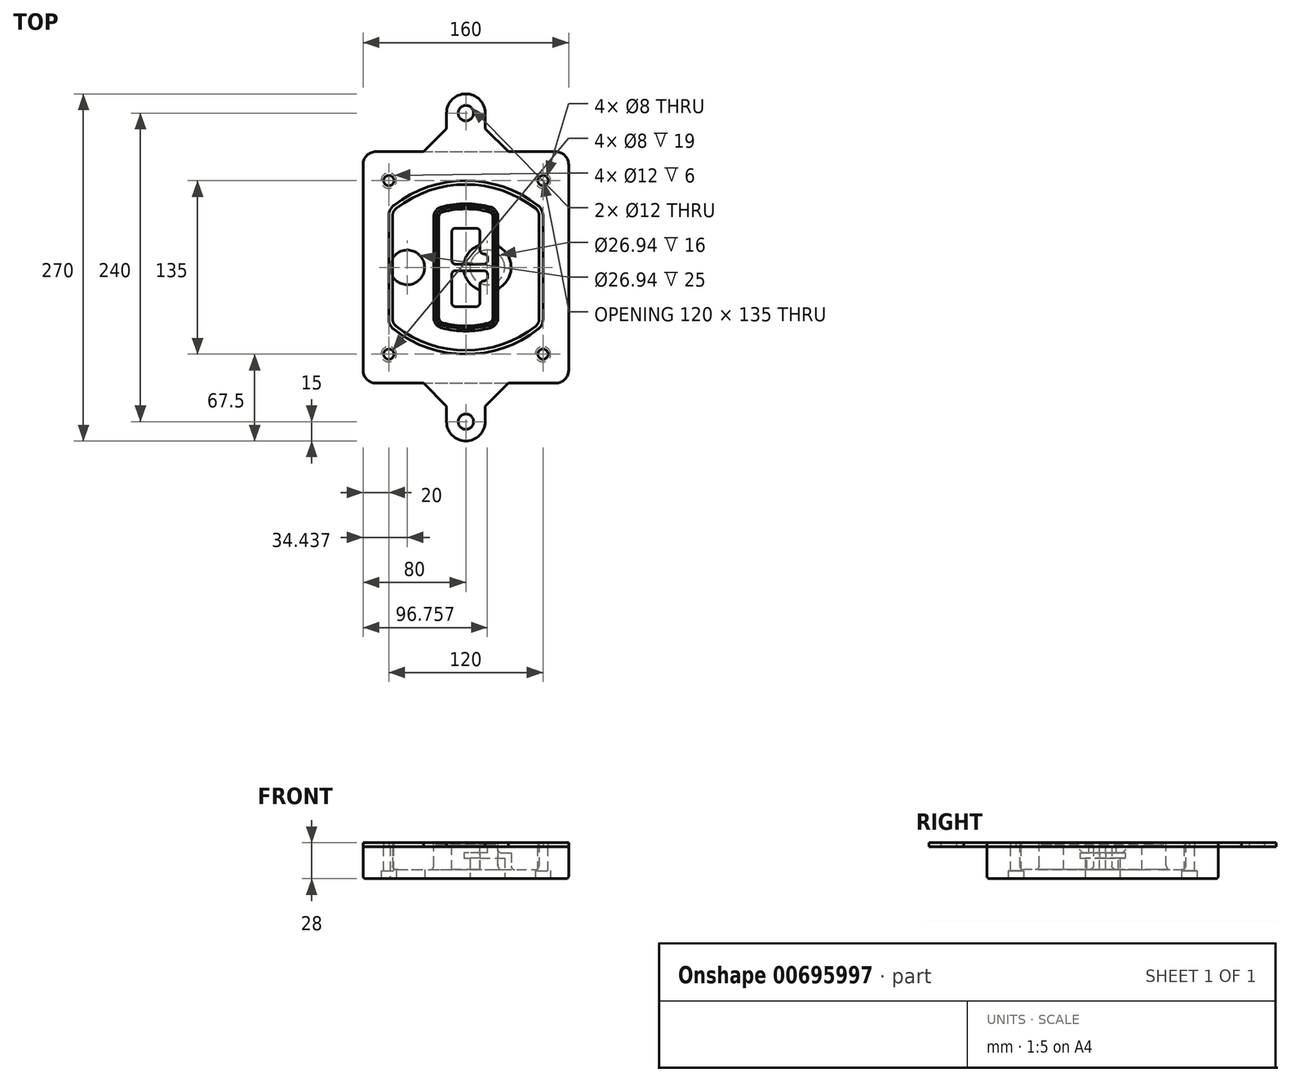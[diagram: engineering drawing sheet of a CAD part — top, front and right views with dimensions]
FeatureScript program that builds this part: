
annotation { "Feature Type Name" : "Feature", "Feature Type Description" : "" }
export const myFeature = defineFeature(function(context is Context, id is Id, definition is map)
    precondition{}
    {
        {
            var Q0;
            Q0=qCreatedBy(makeId("Top.planeOp"),FACE);
            var sketch = newSketch(context, id + "F0", { "sketchPlane" : qUnion([Q0])});
            skPoint(sketch, "E0.rect.middle", {"position": v(0, 0) * mm});
            skLineSegment(sketch, "E1.bottom", {"start": v(-70, -90) * mm, "end": v(70, -90) * mm});
            skLineSegment(sketch, "E1.top", {"start": v(-70, 90) * mm, "end": v(70, 90) * mm});
            skLineSegment(sketch, "E1.left", {"start": v(-80, -80) * mm, "end": v(-80, 80) * mm});
            skLineSegment(sketch, "E1.right", {"start": v(80, -80) * mm, "end": v(80, 80) * mm});
            skLineSegment(sketch, "E2", {"start": v(-80, 90) * mm, "end": v(80, -90) * mm, "construction": true});
            skLineSegment(sketch, "E3", {"start": v(80, 90) * mm, "end": v(-80, -90) * mm, "construction": true});
            skCircle(sketch, "E4", {"center": v(-60, 67.5) * mm, "radius": 4 * mm});
            skCircle(sketch, "E5", {"center": v(60, 67.5) * mm, "radius": 4 * mm});
            skCircle(sketch, "E6", {"center": v(60, -67.5) * mm, "radius": 4 * mm});
            skCircle(sketch, "E7", {"center": v(-60, -67.5) * mm, "radius": 4 * mm});
            skLineSegment(sketch, "E8", {"start": v(-60, 67.5) * mm, "end": v(60, 67.5) * mm, "construction": true});
            skLineSegment(sketch, "E9", {"start": v(60, 67.5) * mm, "end": v(60, -67.5) * mm, "construction": true});
            skLineSegment(sketch, "E10", {"start": v(60, -67.5) * mm, "end": v(-60, -67.5) * mm, "construction": true});
            skLineSegment(sketch, "E11", {"start": v(-60, -67.5) * mm, "end": v(-60, 67.5) * mm, "construction": true});
            skLineSegment(sketch, "E12", {"start": v(-60, 40.3) * mm, "end": v(-60, -40.3) * mm});
            skLineSegment(sketch, "E13", {"start": v(60, 40.3) * mm, "end": v(60, -40.3) * mm});
            skArc(sketch, "E14", {"start": v(56.15, 48.18) * mm, "mid": v(0, 67.5) * mm, "end": v(-56.15, 48.18) * mm});
            skArc(sketch, "E15", {"start": v(-56.15, -48.18) * mm, "mid": v(0, -67.5) * mm, "end": v(56.15, -48.18) * mm});
            skLineSegment(sketch, "E16", {"start": v(-60, 0) * mm, "end": v(60, 0) * mm, "construction": true});
            skPoint(sketch, "E17.visualSharp", {"position": v(-60, -45) * mm});
            skArc(sketch, "E17.filletArc", {"start": v(-60, -40.3) * mm, "mid": v(-58.99, -44.68) * mm, "end": v(-56.15, -48.18) * mm});
            skPoint(sketch, "E18.visualSharp", {"position": v(-60, 45) * mm});
            skArc(sketch, "E18.filletArc", {"start": v(-56.15, 48.18) * mm, "mid": v(-58.99, 44.68) * mm, "end": v(-60, 40.3) * mm});
            skPoint(sketch, "E19.visualSharp", {"position": v(60, 45) * mm});
            skArc(sketch, "E19.filletArc", {"start": v(60, 40.3) * mm, "mid": v(58.99, 44.68) * mm, "end": v(56.15, 48.18) * mm});
            skPoint(sketch, "E20.visualSharp", {"position": v(60, -45) * mm});
            skArc(sketch, "E20.filletArc", {"start": v(56.15, -48.18) * mm, "mid": v(58.99, -44.68) * mm, "end": v(60, -40.3) * mm});
            skPoint(sketch, "E21.visualSharp", {"position": v(-80, 90) * mm});
            skArc(sketch, "E21.filletArc", {"start": v(-70, 90) * mm, "mid": v(-77.07, 87.07) * mm, "end": v(-80, 80) * mm});
            skPoint(sketch, "E22.visualSharp", {"position": v(80, 90) * mm});
            skArc(sketch, "E22.filletArc", {"start": v(80, 80) * mm, "mid": v(77.07, 87.07) * mm, "end": v(70, 90) * mm});
            skPoint(sketch, "E23.visualSharp", {"position": v(80, -90) * mm});
            skArc(sketch, "E23.filletArc", {"start": v(70, -90) * mm, "mid": v(77.07, -87.07) * mm, "end": v(80, -80) * mm});
            skPoint(sketch, "E24.visualSharp", {"position": v(-80, -90) * mm});
            skArc(sketch, "E24.filletArc", {"start": v(-80, -80) * mm, "mid": v(-77.07, -87.07) * mm, "end": v(-70, -90) * mm});
            skArc(sketch, "E25.0", {"start": v(57, 40.3) * mm, "mid": v(56.3, 43.36) * mm, "end": v(54.3, 45.81) * mm});
            skLineSegment(sketch, "E25.1", {"start": v(57, 40.3) * mm, "end": v(57, -40.3) * mm});
            skArc(sketch, "E25.2", {"start": v(54.3, -45.81) * mm, "mid": v(56.3, -43.36) * mm, "end": v(57, -40.3) * mm});
            skArc(sketch, "E25.3", {"start": v(-54.3, -45.81) * mm, "mid": v(0, -64.5) * mm, "end": v(54.3, -45.81) * mm});
            skArc(sketch, "E25.4", {"start": v(-57, -40.3) * mm, "mid": v(-56.3, -43.36) * mm, "end": v(-54.3, -45.81) * mm});
            skArc(sketch, "E25.5", {"start": v(54.3, 45.81) * mm, "mid": v(0, 64.5) * mm, "end": v(-54.3, 45.81) * mm});
            skLineSegment(sketch, "E25.6", {"start": v(-57, 40.3) * mm, "end": v(-57, -40.3) * mm});
            skArc(sketch, "E25.7", {"start": v(-54.3, 45.81) * mm, "mid": v(-56.3, 43.36) * mm, "end": v(-57, 40.3) * mm});
            skArc(sketch, "E26.0", {"start": v(-58.62, 51.33) * mm, "mid": v(-62.58, 46.43) * mm, "end": v(-64, 40.3) * mm});
            skArc(sketch, "E26.1", {"start": v(58.62, 51.33) * mm, "mid": v(0, 71.5) * mm, "end": v(-58.62, 51.33) * mm});
            skArc(sketch, "E26.2", {"start": v(64, 40.3) * mm, "mid": v(62.58, 46.43) * mm, "end": v(58.62, 51.33) * mm});
            skLineSegment(sketch, "E26.3", {"start": v(64, 40.3) * mm, "end": v(64, -40.3) * mm});
            skArc(sketch, "E26.4", {"start": v(58.62, -51.33) * mm, "mid": v(62.58, -46.43) * mm, "end": v(64, -40.3) * mm});
            skLineSegment(sketch, "E26.5", {"start": v(-64, 40.3) * mm, "end": v(-64, -40.3) * mm});
            skArc(sketch, "E26.6", {"start": v(-58.62, -51.33) * mm, "mid": v(0, -71.5) * mm, "end": v(58.62, -51.33) * mm});
            skArc(sketch, "E26.7", {"start": v(-64, -40.3) * mm, "mid": v(-62.58, -46.43) * mm, "end": v(-58.62, -51.33) * mm});
            skSolve(sketch);
        }
        {
            var Q0;
            Q0=makeQuery(id+"F0.imprint","IMPRINT",FACE,{"disambiguationData":[TD([[makeQuery(id+"F0.imprint","IMPRINT",EDGE,{"derivedFrom":sQuery(id+"F0.wireOp",EDGE,"E1.bottom")}),1.0]])]});
            var Q1;
            Q1=makeQuery(id+"F0.imprint","IMPRINT",FACE,{"disambiguationData":[TD([[makeQuery(id+"F0.imprint","IMPRINT",EDGE,{"derivedFrom":sQuery(id+"F0.wireOp",EDGE,"E12")}),1.0]])]});
            var Q2;
            Q2=makeQuery(id+"F0.imprint","IMPRINT",FACE,{"disambiguationData":[TD([[makeQuery(id+"F0.imprint","IMPRINT",EDGE,{"derivedFrom":sQuery(id+"F0.wireOp",EDGE,"E25.0")}),1.0]])]});
            var Q3;
            Q3=makeQuery(id+"F0.imprint","IMPRINT",FACE,{"disambiguationData":[TD([[makeQuery(id+"F0.imprint","IMPRINT",EDGE,{"derivedFrom":sQuery(id+"F0.wireOp",EDGE,"E12")}),-1.0]])]});
            extrude(context, id + "F1", {"entities" : qUnion([Q0, Q1, Q2, Q3]), "oppositeDirection" : true, "depth" : 25 * mm});
        }
        {
            var Q0;
            Q0=makeQuery(id+"F0.imprint","IMPRINT",FACE,{"disambiguationData":[TD([[makeQuery(id+"F0.imprint","IMPRINT",EDGE,{"derivedFrom":sQuery(id+"F0.wireOp",EDGE,"E12")}),1.0]])]});
            extrude(context, id + "F2", {"entities" : qUnion([Q0]), "operationType" : NewBodyOperationType.ADD, "depth" : 3 * mm});
        }
        {
            var Q0;
            Q0=makeQuery(id+"F0.imprint","IMPRINT",FACE,{"disambiguationData":[TD([[makeQuery(id+"F0.imprint","IMPRINT",EDGE,{"derivedFrom":sQuery(id+"F0.wireOp",EDGE,"E25.0")}),1.0]])]});
            extrude(context, id + "F3", {"entities" : qUnion([Q0]), "operationType" : NewBodyOperationType.REMOVE, "oppositeDirection" : true, "depth" : 18 * mm});
        }
        {
            var Q0;
            Q0=makeQuery(id+"F2.opExtrude","CAP_FACE",FACE,{"disambiguationData":[OSD([sQuery(id+"F0.wireOp",EDGE,"E12"),sQuery(id+"F0.wireOp",EDGE,"E13"),sQuery(id+"F0.wireOp",EDGE,"E14"),sQuery(id+"F0.wireOp",EDGE,"E15"),sQuery(id+"F0.wireOp",EDGE,"E17.filletArc"),sQuery(id+"F0.wireOp",EDGE,"E18.filletArc"),sQuery(id+"F0.wireOp",EDGE,"E19.filletArc"),sQuery(id+"F0.wireOp",EDGE,"E20.filletArc"),sQuery(id+"F0.wireOp",EDGE,"E25.0"),sQuery(id+"F0.wireOp",EDGE,"E25.1"),sQuery(id+"F0.wireOp",EDGE,"E25.2"),sQuery(id+"F0.wireOp",EDGE,"E25.3"),sQuery(id+"F0.wireOp",EDGE,"E25.4"),sQuery(id+"F0.wireOp",EDGE,"E25.5"),sQuery(id+"F0.wireOp",EDGE,"E25.6"),sQuery(id+"F0.wireOp",EDGE,"E25.7")])],"isStart":false});
            var sketch = newSketch(context, id + "F4", { "sketchPlane" : qUnion([Q0])});
            skArc(sketch, "E27.0", {"start": v(-19.08, -46.97) * mm, "mid": v(0, -49.5) * mm, "end": v(19.08, -46.97) * mm});
            skArc(sketch, "E28.0", {"start": v(19.08, 46.97) * mm, "mid": v(0, 49.5) * mm, "end": v(-19.08, 46.97) * mm});
            skLineSegment(sketch, "E29", {"start": v(-25, 39.25) * mm, "end": v(-25, -39.25) * mm});
            skLineSegment(sketch, "E30", {"start": v(25, 39.25) * mm, "end": v(25, -39.25) * mm});
            skLineSegment(sketch, "E31", {"start": v(-25, 45.1) * mm, "end": v(25, 45.1) * mm, "construction": true});
            skLineSegment(sketch, "E32", {"start": v(-25, -45.1) * mm, "end": v(25, -45.1) * mm, "construction": true});
            skPoint(sketch, "E33.visualSharp", {"position": v(-25, 45.1) * mm});
            skArc(sketch, "E33.filletArc", {"start": v(-19.08, 46.97) * mm, "mid": v(-23.35, 44.11) * mm, "end": v(-25, 39.25) * mm});
            skPoint(sketch, "E34.visualSharp", {"position": v(25, 45.1) * mm});
            skArc(sketch, "E34.filletArc", {"start": v(25, 39.25) * mm, "mid": v(23.35, 44.11) * mm, "end": v(19.08, 46.97) * mm});
            skPoint(sketch, "E35.visualSharp", {"position": v(25, -45.1) * mm});
            skArc(sketch, "E35.filletArc", {"start": v(19.08, -46.97) * mm, "mid": v(23.35, -44.11) * mm, "end": v(25, -39.25) * mm});
            skPoint(sketch, "E36.visualSharp", {"position": v(-25, -45.1) * mm});
            skArc(sketch, "E36.filletArc", {"start": v(-25, -39.25) * mm, "mid": v(-23.35, -44.11) * mm, "end": v(-19.08, -46.97) * mm});
            skArc(sketch, "E37.0", {"start": v(54.3, 45.81) * mm, "mid": v(0, 64.5) * mm, "end": v(-54.3, 45.81) * mm});
            skArc(sketch, "E37.1", {"start": v(-54.3, 45.81) * mm, "mid": v(-56.3, 43.36) * mm, "end": v(-57, 40.3) * mm});
            skLineSegment(sketch, "E37.2", {"start": v(-57, 40.3) * mm, "end": v(-57, -40.3) * mm});
            skArc(sketch, "E37.3", {"start": v(-57, -40.3) * mm, "mid": v(-56.3, -43.36) * mm, "end": v(-54.3, -45.81) * mm});
            skArc(sketch, "E37.4", {"start": v(-54.3, -45.81) * mm, "mid": v(0, -64.5) * mm, "end": v(54.3, -45.81) * mm});
            skArc(sketch, "E37.5", {"start": v(54.3, -45.81) * mm, "mid": v(56.3, -43.36) * mm, "end": v(57, -40.3) * mm});
            skLineSegment(sketch, "E37.6", {"start": v(57, 40.3) * mm, "end": v(57, -40.3) * mm});
            skArc(sketch, "E37.7", {"start": v(57, 40.3) * mm, "mid": v(56.3, 43.36) * mm, "end": v(54.3, 45.81) * mm});
            skLineSegment(sketch, "E38.0", {"start": v(23, 39.25) * mm, "end": v(23, -39.25) * mm});
            skArc(sketch, "E38.1", {"start": v(18.56, -45.04) * mm, "mid": v(21.76, -42.9) * mm, "end": v(23, -39.25) * mm});
            skArc(sketch, "E38.2", {"start": v(-18.56, -45.04) * mm, "mid": v(0, -47.5) * mm, "end": v(18.56, -45.04) * mm});
            skArc(sketch, "E38.3", {"start": v(-23, -39.25) * mm, "mid": v(-21.76, -42.9) * mm, "end": v(-18.56, -45.04) * mm});
            skLineSegment(sketch, "E38.4", {"start": v(-23, 39.25) * mm, "end": v(-23, -39.25) * mm});
            skArc(sketch, "E38.5", {"start": v(23, 39.25) * mm, "mid": v(21.76, 42.9) * mm, "end": v(18.56, 45.04) * mm});
            skArc(sketch, "E38.6", {"start": v(-18.56, 45.04) * mm, "mid": v(-21.76, 42.9) * mm, "end": v(-23, 39.25) * mm});
            skArc(sketch, "E38.7", {"start": v(18.56, 45.04) * mm, "mid": v(0, 47.5) * mm, "end": v(-18.56, 45.04) * mm});
            skArc(sketch, "E39.0", {"start": v(21, 39.25) * mm, "mid": v(20.18, 41.68) * mm, "end": v(18.04, 43.1) * mm});
            skLineSegment(sketch, "E39.1", {"start": v(21, 39.25) * mm, "end": v(21, -39.25) * mm});
            skArc(sketch, "E39.2", {"start": v(18.04, -43.1) * mm, "mid": v(20.18, -41.68) * mm, "end": v(21, -39.25) * mm});
            skArc(sketch, "E39.3", {"start": v(-18.04, -43.1) * mm, "mid": v(0, -45.5) * mm, "end": v(18.04, -43.1) * mm});
            skArc(sketch, "E39.4", {"start": v(-21, -39.25) * mm, "mid": v(-20.18, -41.68) * mm, "end": v(-18.04, -43.1) * mm});
            skArc(sketch, "E39.5", {"start": v(18.04, 43.1) * mm, "mid": v(0, 45.5) * mm, "end": v(-18.04, 43.1) * mm});
            skLineSegment(sketch, "E39.6", {"start": v(-21, 39.25) * mm, "end": v(-21, -39.25) * mm});
            skArc(sketch, "E39.7", {"start": v(-18.04, 43.1) * mm, "mid": v(-20.18, 41.68) * mm, "end": v(-21, 39.25) * mm});
            skLineSegment(sketch, "E40", {"start": v(-25, 0) * mm, "end": v(25, 0) * mm, "construction": true});
            skLineSegment(sketch, "E41", {"start": v(-11, 5.5) * mm, "end": v(-11, 27.5) * mm});
            skLineSegment(sketch, "E42", {"start": v(-8, 30.5) * mm, "end": v(8, 30.5) * mm});
            skLineSegment(sketch, "E43", {"start": v(11, 27.5) * mm, "end": v(11, 13.5) * mm});
            skLineSegment(sketch, "E44", {"start": v(14, 10.5) * mm, "end": v(14, 10.5) * mm});
            skLineSegment(sketch, "E45", {"start": v(17, 7.5) * mm, "end": v(17, 5.5) * mm});
            skLineSegment(sketch, "E46", {"start": v(14, 2.5) * mm, "end": v(-8, 2.5) * mm});
            skPoint(sketch, "E47.visualSharp", {"position": v(-11, 30.5) * mm});
            skArc(sketch, "E47.filletArc", {"start": v(-8, 30.5) * mm, "mid": v(-10.12, 29.62) * mm, "end": v(-11, 27.5) * mm});
            skPoint(sketch, "E48.visualSharp", {"position": v(11, 30.5) * mm});
            skArc(sketch, "E48.filletArc", {"start": v(11, 27.5) * mm, "mid": v(10.12, 29.62) * mm, "end": v(8, 30.5) * mm});
            skPoint(sketch, "E49.visualSharp", {"position": v(11, 10.5) * mm});
            skArc(sketch, "E49.filletArc", {"start": v(11, 13.5) * mm, "mid": v(11.88, 11.38) * mm, "end": v(14, 10.5) * mm});
            skPoint(sketch, "E50.visualSharp", {"position": v(17, 10.5) * mm});
            skArc(sketch, "E50.filletArc", {"start": v(17, 7.5) * mm, "mid": v(16.12, 9.62) * mm, "end": v(14, 10.5) * mm});
            skPoint(sketch, "E51.visualSharp", {"position": v(17, 2.5) * mm});
            skArc(sketch, "E51.filletArc", {"start": v(14, 2.5) * mm, "mid": v(16.12, 3.38) * mm, "end": v(17, 5.5) * mm});
            skPoint(sketch, "E52.visualSharp", {"position": v(-11, 2.5) * mm});
            skArc(sketch, "E52.filletArc", {"start": v(-11, 5.5) * mm, "mid": v(-10.12, 3.38) * mm, "end": v(-8, 2.5) * mm});
            skLineSegment(sketch, "E53.0.MirrorCS", {"start": v(14, -2.5) * mm, "end": v(-8, -2.5) * mm});
            skArc(sketch, "E54.0.MirrorCS", {"start": v(-11, -5.5) * mm, "mid": v(-10.12, -3.38) * mm, "end": v(-8, -2.5) * mm});
            skLineSegment(sketch, "E55.0.MirrorCS", {"start": v(-11, -5.5) * mm, "end": v(-11, -27.5) * mm});
            skArc(sketch, "E56.0.MirrorCS", {"start": v(-8, -30.5) * mm, "mid": v(-10.12, -29.62) * mm, "end": v(-11, -27.5) * mm});
            skLineSegment(sketch, "E57.0.MirrorCS", {"start": v(-8, -30.5) * mm, "end": v(8, -30.5) * mm});
            skArc(sketch, "E58.0.MirrorCS", {"start": v(11, -27.5) * mm, "mid": v(10.12, -29.62) * mm, "end": v(8, -30.5) * mm});
            skLineSegment(sketch, "E59.0.MirrorCS", {"start": v(11, -27.5) * mm, "end": v(11, -13.5) * mm});
            skArc(sketch, "E60.0.MirrorCS", {"start": v(11, -13.5) * mm, "mid": v(11.88, -11.38) * mm, "end": v(14, -10.5) * mm});
            skArc(sketch, "E61.0.MirrorCS", {"start": v(17, -7.5) * mm, "mid": v(16.12, -9.62) * mm, "end": v(14, -10.5) * mm});
            skLineSegment(sketch, "E62.0.MirrorCS", {"start": v(17, -7.5) * mm, "end": v(17, -5.5) * mm});
            skArc(sketch, "E63.0.MirrorCS", {"start": v(14, -2.5) * mm, "mid": v(16.12, -3.38) * mm, "end": v(17, -5.5) * mm});
            skSolve(sketch);
        }
        {
            var Q0;
            Q0=makeQuery(id+"F4.imprint","IMPRINT",FACE,{"disambiguationData":[TD([[makeQuery(id+"F4.imprint","IMPRINT",EDGE,{"derivedFrom":sQuery(id+"F4.wireOp",EDGE,"E27.0")}),1.0]])]});
            var Q1;
            Q1=makeQuery(id+"F4.imprint","IMPRINT",FACE,{"disambiguationData":[TD([[makeQuery(id+"F4.imprint","IMPRINT",EDGE,{"derivedFrom":sQuery(id+"F4.wireOp",EDGE,"E38.0")}),-1.0]])]});
            var Q2;
            Q2=makeQuery(id+"F4.imprint","IMPRINT",FACE,{"disambiguationData":[TD([[makeQuery(id+"F4.imprint","IMPRINT",EDGE,{"derivedFrom":sQuery(id+"F4.wireOp",EDGE,"E39.0")}),1.0]])]});
            extrude(context, id + "F5", {"entities" : qUnion([Q0, Q1, Q2]), "operationType" : NewBodyOperationType.ADD, "endBound" : BoundingType.UP_TO_NEXT, "oppositeDirection" : true, "depth" : 25 * mm});
        }
        {
            var Q0;
            Q0=makeQuery(id+"F4.imprint","IMPRINT",FACE,{"disambiguationData":[TD([[makeQuery(id+"F4.imprint","IMPRINT",EDGE,{"derivedFrom":sQuery(id+"F4.wireOp",EDGE,"E38.0")}),-1.0]])]});
            extrude(context, id + "F6", {"entities" : qUnion([Q0]), "operationType" : NewBodyOperationType.REMOVE, "oppositeDirection" : true, "depth" : 2 * mm});
        }
        {
            var Q0;
            Q0=makeQuery(id+"F1.opExtrude","CAP_FACE",FACE,{"disambiguationData":[OSD([sQuery(id+"F0.wireOp",EDGE,"E1.bottom"),sQuery(id+"F0.wireOp",EDGE,"E1.top"),sQuery(id+"F0.wireOp",EDGE,"E1.left"),sQuery(id+"F0.wireOp",EDGE,"E1.right"),sQuery(id+"F0.wireOp",EDGE,"E4"),sQuery(id+"F0.wireOp",EDGE,"E5"),sQuery(id+"F0.wireOp",EDGE,"E6"),sQuery(id+"F0.wireOp",EDGE,"E7"),sQuery(id+"F0.wireOp",EDGE,"E21.filletArc"),sQuery(id+"F0.wireOp",EDGE,"E22.filletArc"),sQuery(id+"F0.wireOp",EDGE,"E23.filletArc"),sQuery(id+"F0.wireOp",EDGE,"E24.filletArc")])],"isStart":false});
            var sketch = newSketch(context, id + "F7", { "sketchPlane" : qUnion([Q0])});
            skCircle(sketch, "E64", {"center": v(16.76, 0) * mm, "radius": 13.47 * mm});
            skCircle(sketch, "E65", {"center": v(-45.56, 0) * mm, "radius": 13.47 * mm});
            skLineSegment(sketch, "E66", {"start": v(80, 0) * mm, "end": v(-80, 0) * mm});
            skCircle(sketch, "E67", {"center": v(16.76, 0) * mm, "radius": 18.47 * mm});
            skCircle(sketch, "E68", {"center": v(60, -67.5) * mm, "radius": 6 * mm});
            skCircle(sketch, "E69", {"center": v(-60, -67.5) * mm, "radius": 6 * mm});
            skCircle(sketch, "E70", {"center": v(-60, 67.5) * mm, "radius": 6 * mm});
            skCircle(sketch, "E71", {"center": v(60, 67.5) * mm, "radius": 6 * mm});
            skSolve(sketch);
        }
        {
            var Q0;
            {var subQ1=sQuery(id+"F7.wireOp",EDGE,"E66");var subQ4=sQuery(id+"F7.wireOp",EDGE,"E64");var subQ6=makeQuery(id+"F7.imprint","INTERSECT",VERTEX,{"disambiguationData":[OD(0.0)],"derivedFrom":[subQ4,subQ1]});Q0=makeQuery(id+"F7.imprint","IMPRINT",FACE,{"disambiguationData":[TD([[makeQuery(id+"F7.imprint","IMPRINT",EDGE,{"disambiguationData":[TD([[subQ6,-1.0]])],"derivedFrom":subQ4}),-1.0]])]});}
            var Q1;
            {var subQ0=sQuery(id+"F7.wireOp",EDGE,"E66");var subQ1=sQuery(id+"F7.wireOp",EDGE,"E64");var subQ3=makeQuery(id+"F7.imprint","INTERSECT",VERTEX,{"disambiguationData":[OD(0.0)],"derivedFrom":[subQ1,subQ0]});Q1=makeQuery(id+"F7.imprint","IMPRINT",FACE,{"disambiguationData":[TD([[makeQuery(id+"F7.imprint","IMPRINT",EDGE,{"disambiguationData":[TD([[subQ3,-1.0]])],"derivedFrom":subQ1}),1.0]])]});}
            var Q2;
            {var subQ0=sQuery(id+"F7.wireOp",EDGE,"E66");var subQ1=sQuery(id+"F7.wireOp",EDGE,"E64");var subQ3=makeQuery(id+"F7.imprint","INTERSECT",VERTEX,{"disambiguationData":[OD(0.0)],"derivedFrom":[subQ1,subQ0]});Q2=makeQuery(id+"F7.imprint","IMPRINT",FACE,{"disambiguationData":[TD([[makeQuery(id+"F7.imprint","IMPRINT",EDGE,{"disambiguationData":[TD([[subQ3,1.0]])],"derivedFrom":subQ1}),1.0]])]});}
            var Q3;
            {var subQ1=sQuery(id+"F7.wireOp",EDGE,"E66");var subQ4=sQuery(id+"F7.wireOp",EDGE,"E64");var subQ6=makeQuery(id+"F7.imprint","INTERSECT",VERTEX,{"disambiguationData":[OD(0.0)],"derivedFrom":[subQ4,subQ1]});Q3=makeQuery(id+"F7.imprint","IMPRINT",FACE,{"disambiguationData":[TD([[makeQuery(id+"F7.imprint","IMPRINT",EDGE,{"disambiguationData":[TD([[subQ6,1.0]])],"derivedFrom":subQ4}),-1.0]])]});}
            extrude(context, id + "F8", {"entities" : qUnion([Q0, Q1, Q2, Q3]), "operationType" : NewBodyOperationType.ADD, "oppositeDirection" : true, "depth" : 20 * mm});
        }
        {
            var Q0;
            {var subQ0=sQuery(id+"F7.wireOp",EDGE,"E66");var subQ1=sQuery(id+"F7.wireOp",EDGE,"E64");var subQ3=makeQuery(id+"F7.imprint","INTERSECT",VERTEX,{"disambiguationData":[OD(0.0)],"derivedFrom":[subQ1,subQ0]});Q0=makeQuery(id+"F7.imprint","IMPRINT",FACE,{"disambiguationData":[TD([[makeQuery(id+"F7.imprint","IMPRINT",EDGE,{"disambiguationData":[TD([[subQ3,-1.0]])],"derivedFrom":subQ1}),1.0]])]});}
            var Q1;
            {var subQ0=sQuery(id+"F7.wireOp",EDGE,"E66");var subQ1=sQuery(id+"F7.wireOp",EDGE,"E64");var subQ3=makeQuery(id+"F7.imprint","INTERSECT",VERTEX,{"disambiguationData":[OD(0.0)],"derivedFrom":[subQ1,subQ0]});Q1=makeQuery(id+"F7.imprint","IMPRINT",FACE,{"disambiguationData":[TD([[makeQuery(id+"F7.imprint","IMPRINT",EDGE,{"disambiguationData":[TD([[subQ3,1.0]])],"derivedFrom":subQ1}),1.0]])]});}
            extrude(context, id + "F9", {"entities" : qUnion([Q0, Q1]), "operationType" : NewBodyOperationType.REMOVE, "oppositeDirection" : true, "depth" : 16 * mm});
        }
        {
            var Q0;
            {var subQ0=sQuery(id+"F7.wireOp",EDGE,"E66");var subQ1=sQuery(id+"F7.wireOp",EDGE,"E65");var subQ3=makeQuery(id+"F7.imprint","INTERSECT",VERTEX,{"disambiguationData":[OD(0.0)],"derivedFrom":[subQ1,subQ0]});Q0=makeQuery(id+"F7.imprint","IMPRINT",FACE,{"disambiguationData":[TD([[makeQuery(id+"F7.imprint","IMPRINT",EDGE,{"disambiguationData":[TD([[subQ3,-1.0]])],"derivedFrom":subQ1}),1.0]])]});}
            var Q1;
            {var subQ0=sQuery(id+"F7.wireOp",EDGE,"E66");var subQ1=sQuery(id+"F7.wireOp",EDGE,"E65");var subQ3=makeQuery(id+"F7.imprint","INTERSECT",VERTEX,{"disambiguationData":[OD(0.0)],"derivedFrom":[subQ1,subQ0]});Q1=makeQuery(id+"F7.imprint","IMPRINT",FACE,{"disambiguationData":[TD([[makeQuery(id+"F7.imprint","IMPRINT",EDGE,{"disambiguationData":[TD([[subQ3,1.0]])],"derivedFrom":subQ1}),1.0]])]});}
            extrude(context, id + "F10", {"entities" : qUnion([Q0, Q1]), "operationType" : NewBodyOperationType.REMOVE, "oppositeDirection" : true, "depth" : 25 * mm});
        }
        {
            var Q0;
            Q0=makeQuery(id+"F7.imprint","IMPRINT",FACE,{"disambiguationData":[TD([[makeQuery(id+"F7.imprint","IMPRINT",EDGE,{"derivedFrom":sQuery(id+"F7.wireOp",EDGE,"E68")}),1.0]])]});
            var Q1;
            Q1=makeQuery(id+"F7.imprint","IMPRINT",FACE,{"disambiguationData":[TD([[makeQuery(id+"F7.imprint","IMPRINT",EDGE,{"derivedFrom":makeQuery(id+"F1.opExtrude","CAP_EDGE",EDGE,{"disambiguationData":[OSD([sQuery(id+"F0.wireOp",EDGE,"E5")])],"isStart":false})}),-1.0]])]});
            var Q2;
            Q2=makeQuery(id+"F7.imprint","IMPRINT",FACE,{"disambiguationData":[TD([[makeQuery(id+"F7.imprint","IMPRINT",EDGE,{"derivedFrom":sQuery(id+"F7.wireOp",EDGE,"E69")}),1.0]])]});
            var Q3;
            Q3=makeQuery(id+"F7.imprint","IMPRINT",FACE,{"disambiguationData":[TD([[makeQuery(id+"F7.imprint","IMPRINT",EDGE,{"derivedFrom":makeQuery(id+"F1.opExtrude","CAP_EDGE",EDGE,{"disambiguationData":[OSD([sQuery(id+"F0.wireOp",EDGE,"E4")])],"isStart":false})}),-1.0]])]});
            var Q4;
            Q4=makeQuery(id+"F7.imprint","IMPRINT",FACE,{"disambiguationData":[TD([[makeQuery(id+"F7.imprint","IMPRINT",EDGE,{"derivedFrom":sQuery(id+"F7.wireOp",EDGE,"E70")}),1.0]])]});
            var Q5;
            Q5=makeQuery(id+"F7.imprint","IMPRINT",FACE,{"disambiguationData":[TD([[makeQuery(id+"F7.imprint","IMPRINT",EDGE,{"derivedFrom":makeQuery(id+"F1.opExtrude","CAP_EDGE",EDGE,{"disambiguationData":[OSD([sQuery(id+"F0.wireOp",EDGE,"E7")])],"isStart":false})}),-1.0]])]});
            var Q6;
            Q6=makeQuery(id+"F7.imprint","IMPRINT",FACE,{"disambiguationData":[TD([[makeQuery(id+"F7.imprint","IMPRINT",EDGE,{"derivedFrom":sQuery(id+"F7.wireOp",EDGE,"E71")}),1.0]])]});
            var Q7;
            Q7=makeQuery(id+"F7.imprint","IMPRINT",FACE,{"disambiguationData":[TD([[makeQuery(id+"F7.imprint","IMPRINT",EDGE,{"derivedFrom":makeQuery(id+"F1.opExtrude","CAP_EDGE",EDGE,{"disambiguationData":[OSD([sQuery(id+"F0.wireOp",EDGE,"E6")])],"isStart":false})}),-1.0]])]});
            extrude(context, id + "F11", {"entities" : qUnion([Q0, Q1, Q2, Q3, Q4, Q5, Q6, Q7]), "operationType" : NewBodyOperationType.REMOVE, "oppositeDirection" : true, "depth" : 6 * mm});
        }
        {
            var Q0;
            Q0=makeQuery(id+"F9.boolean.opBoolean","COPY",FACE,{"derivedFrom":makeQuery(id+"F9.opExtrude","CAP_FACE",FACE,{"disambiguationData":[OSD([sQuery(id+"F7.wireOp",EDGE,"E64")])],"isStart":false})});
            var sketch = newSketch(context, id + "F12", { "sketchPlane" : qUnion([Q0])});
            skArc(sketch, "E72.0", {"start": v(11, 17.55) * mm, "mid": v(2.57, 11.82) * mm, "end": v(-1.54, 2.5) * mm});
            skArc(sketch, "E72.1", {"start": v(-1.54, -2.5) * mm, "mid": v(2.57, -11.82) * mm, "end": v(11, -17.55) * mm});
            skLineSegment(sketch, "E73", {"start": v(-1.54, -2.5) * mm, "end": v(14, -2.5) * mm});
            skLineSegment(sketch, "E74.0", {"start": v(14, 2.5) * mm, "end": v(-1.54, 2.5) * mm});
            skArc(sketch, "E74.1", {"start": v(14, 2.5) * mm, "mid": v(16.12, 3.38) * mm, "end": v(17, 5.5) * mm});
            skLineSegment(sketch, "E74.2", {"start": v(17, 7.5) * mm, "end": v(17, 5.5) * mm});
            skArc(sketch, "E74.3", {"start": v(17, 7.5) * mm, "mid": v(16.12, 9.62) * mm, "end": v(14, 10.5) * mm});
            skArc(sketch, "E74.4", {"start": v(11, 13.5) * mm, "mid": v(11.88, 11.38) * mm, "end": v(14, 10.5) * mm});
            skLineSegment(sketch, "E74.5", {"start": v(11, 17.55) * mm, "end": v(11, 13.5) * mm});
            skLineSegment(sketch, "E74.7", {"start": v(14, -2.5) * mm, "end": v(-1.54, -2.5) * mm});
            skArc(sketch, "E74.8", {"start": v(14, -2.5) * mm, "mid": v(16.12, -3.38) * mm, "end": v(17, -5.5) * mm});
            skLineSegment(sketch, "E74.9", {"start": v(17, -7.5) * mm, "end": v(17, -5.5) * mm});
            skArc(sketch, "E74.10", {"start": v(17, -7.5) * mm, "mid": v(16.12, -9.62) * mm, "end": v(14, -10.5) * mm});
            skArc(sketch, "E74.11", {"start": v(11, -13.5) * mm, "mid": v(11.88, -11.38) * mm, "end": v(14, -10.5) * mm});
            skLineSegment(sketch, "E74.12", {"start": v(11, -17.55) * mm, "end": v(11, -13.5) * mm});
            skPoint(sketch, "E75.orphan", {"position": v(11, -27.5) * mm});
            skPoint(sketch, "E76.orphan", {"position": v(-8, -2.5) * mm});
            skPoint(sketch, "E77.orphan", {"position": v(-8, 2.5) * mm});
            skPoint(sketch, "E78.orphan", {"position": v(11, 27.5) * mm});
            skSolve(sketch);
        }
        {
            var Q0;
            {var subQ7=sQuery(id+"F12.wireOp",EDGE,"E72.0");var subQ14=sQuery(id+"F12.wireOp",EDGE,"E72.1");var subQ16=sQuery(id+"F12.wireOp",EDGE,"E74.1");var subQ18=sQuery(id+"F12.wireOp",EDGE,"E74.8");Q0=qUnion([makeQuery(id+"F12.imprint","IMPRINT",FACE,{"disambiguationData":[TD([[makeQuery(id+"F12.imprint","IMPRINT",EDGE,{"derivedFrom":subQ7}),1.0]])]}),makeQuery(id+"F12.imprint","IMPRINT",FACE,{"disambiguationData":[TD([[makeQuery(id+"F12.imprint","IMPRINT",EDGE,{"derivedFrom":subQ14}),1.0]])]}),makeQuery(id+"F12.imprint","IMPRINT",FACE,{"disambiguationData":[TD([[makeQuery(id+"F12.imprint","IMPRINT",EDGE,{"derivedFrom":subQ16}),1.0]])]}),makeQuery(id+"F12.imprint","IMPRINT",FACE,{"disambiguationData":[TD([[makeQuery(id+"F12.imprint","IMPRINT",EDGE,{"derivedFrom":subQ18}),-1.0]])]})]);}
            var Q1;
            Q1=makeQuery(id+"F5.boolean.opBoolean","SPLIT",FACE,{"disambiguationData":[TD([makeQuery(id+"F5.opExtrude","SWEPT_FACE",FACE,{"disambiguationData":[OSD([sQuery(id+"F4.wireOp",EDGE,"E41")])]})])],"derivedFrom":makeQuery(id+"F3.boolean.opBoolean","COPY",FACE,{"derivedFrom":makeQuery(id+"F3.opExtrude","CAP_FACE",FACE,{"disambiguationData":[OSD([sQuery(id+"F0.wireOp",EDGE,"E25.0"),sQuery(id+"F0.wireOp",EDGE,"E25.1"),sQuery(id+"F0.wireOp",EDGE,"E25.2"),sQuery(id+"F0.wireOp",EDGE,"E25.3"),sQuery(id+"F0.wireOp",EDGE,"E25.4"),sQuery(id+"F0.wireOp",EDGE,"E25.5"),sQuery(id+"F0.wireOp",EDGE,"E25.6"),sQuery(id+"F0.wireOp",EDGE,"E25.7")])],"isStart":false})})});
            extrude(context, id + "F13", {"entities" : qUnion([Q0]), "operationType" : NewBodyOperationType.REMOVE, "endBound" : BoundingType.UP_TO_SURFACE, "endBoundEntityFace" : qUnion([Q1]), "depth" : 25 * mm});
        }
        {
            var Q0;
            Q0=makeQuery(id+"F3.boolean.opBoolean","COPY",EDGE,{"derivedFrom":makeQuery(id+"F3.opExtrude","CAP_EDGE",EDGE,{"disambiguationData":[OSD([sQuery(id+"F0.wireOp",EDGE,"E25.6")])],"isStart":false})});
            var Q1;
            Q1=makeQuery(id+"F8.boolean.opBoolean","INTERSECT",EDGE,{"derivedFrom":[makeQuery(id+"F5.opExtrude","SWEPT_FACE",FACE,{"disambiguationData":[OSD([sQuery(id+"F4.wireOp",EDGE,"E30")])]}),makeQuery(id+"F8.opExtrude","CAP_FACE",FACE,{"disambiguationData":[OSD([sQuery(id+"F7.wireOp",EDGE,"E67")])],"isStart":false})]});
            var Q2;
            Q2=makeQuery(id+"F8.boolean.opBoolean","INTERSECT",EDGE,{"disambiguationData":[OD(1.0)],"derivedFrom":[makeQuery(id+"F5.opExtrude","SWEPT_FACE",FACE,{"disambiguationData":[OSD([sQuery(id+"F4.wireOp",EDGE,"E30")])]}),makeQuery(id+"F8.opExtrude","SWEPT_FACE",FACE,{"disambiguationData":[OSD([sQuery(id+"F7.wireOp",EDGE,"E67")])]})]});
            var Q3;
            {var subQ0=sQuery(id+"F4.wireOp",EDGE,"E30");Q3=makeQuery(id+"F8.boolean.opBoolean","SPLIT",EDGE,{"disambiguationData":[TD([makeQuery(id+"F5.opExtrude","SWEPT_FACE",FACE,{"disambiguationData":[OSD([sQuery(id+"F4.wireOp",EDGE,"E35.filletArc")])]})])],"derivedFrom":makeQuery(id+"F5.opExtrude","CAP_EDGE",EDGE,{"disambiguationData":[OSD([subQ0])],"isStart":false})});}
            var Q4;
            {var subQ0=sQuery(id+"F0.wireOp",EDGE,"E25.7");var subQ1=sQuery(id+"F0.wireOp",EDGE,"E25.1");var subQ2=sQuery(id+"F0.wireOp",EDGE,"E25.6");var subQ3=sQuery(id+"F0.wireOp",EDGE,"E25.5");var subQ4=sQuery(id+"F0.wireOp",EDGE,"E25.4");var subQ5=sQuery(id+"F0.wireOp",EDGE,"E25.0");var subQ6=sQuery(id+"F0.wireOp",EDGE,"E25.2");var subQ7=sQuery(id+"F0.wireOp",EDGE,"E25.3");Q4=makeQuery(id+"F8.boolean.opBoolean","INTERSECT",EDGE,{"derivedFrom":[makeQuery(id+"F5.boolean.opBoolean","SPLIT",FACE,{"disambiguationData":[TD([makeQuery(id+"F2.opExtrude","SWEPT_FACE",FACE,{"disambiguationData":[OSD([subQ5])]})])],"derivedFrom":makeQuery(id+"F3.boolean.opBoolean","COPY",FACE,{"derivedFrom":makeQuery(id+"F3.opExtrude","CAP_FACE",FACE,{"disambiguationData":[OSD([subQ5,subQ1,subQ6,subQ7,subQ4,subQ3,subQ2,subQ0])],"isStart":false})})}),makeQuery(id+"F8.opExtrude","SWEPT_FACE",FACE,{"disambiguationData":[OSD([sQuery(id+"F7.wireOp",EDGE,"E67")])]})]});}
            var Q5;
            Q5=makeQuery(id+"F8.boolean.opBoolean","INTERSECT",EDGE,{"disambiguationData":[OD(0.0)],"derivedFrom":[makeQuery(id+"F5.opExtrude","SWEPT_FACE",FACE,{"disambiguationData":[OSD([sQuery(id+"F4.wireOp",EDGE,"E30")])]}),makeQuery(id+"F8.opExtrude","SWEPT_FACE",FACE,{"disambiguationData":[OSD([sQuery(id+"F7.wireOp",EDGE,"E67")])]})]});
            fillet(context, id + "F14", {"entities" : qUnion([Q0, Q1, Q2, Q3, Q4, Q5]), "radius" : 3 * mm, "tangentPropagation" : true, "allowEdgeOverflow" : false});
        }
        {
            var Q0;
            Q0=makeQuery(id+"F1.opExtrude","CAP_EDGE",EDGE,{"disambiguationData":[OSD([sQuery(id+"F0.wireOp",EDGE,"E1.bottom")])],"isStart":false});
            fillet(context, id + "F15", {"entities" : qUnion([Q0]), "radius" : 2 * mm, "tangentPropagation" : true, "allowEdgeOverflow" : false});
        }
        {
            var Q0;
            {var subQ0=sQuery(id+"F0.wireOp",EDGE,"E21.filletArc");var subQ1=sQuery(id+"F0.wireOp",EDGE,"E7");var subQ2=sQuery(id+"F0.wireOp",EDGE,"E6");var subQ3=sQuery(id+"F0.wireOp",EDGE,"E5");var subQ4=sQuery(id+"F0.wireOp",EDGE,"E4");var subQ5=sQuery(id+"F0.wireOp",EDGE,"E22.filletArc");var subQ6=sQuery(id+"F0.wireOp",EDGE,"E1.bottom");var subQ7=sQuery(id+"F0.wireOp",EDGE,"E1.right");var subQ8=sQuery(id+"F0.wireOp",EDGE,"E1.top");var subQ9=sQuery(id+"F0.wireOp",EDGE,"E1.left");var subQ10=sQuery(id+"F0.wireOp",EDGE,"E23.filletArc");var subQ11=sQuery(id+"F0.wireOp",EDGE,"E24.filletArc");Q0=makeQuery(id+"F2.boolean.opBoolean","SPLIT",FACE,{"disambiguationData":[TD([makeQuery(id+"F1.opExtrude","SWEPT_FACE",FACE,{"disambiguationData":[OSD([subQ6])]})])],"derivedFrom":makeQuery(id+"F1.opExtrude","CAP_FACE",FACE,{"disambiguationData":[OSD([subQ6,subQ8,subQ9,subQ7,subQ4,subQ3,subQ2,subQ1,subQ0,subQ5,subQ10,subQ11])],"isStart":true})});}
            var sketch = newSketch(context, id + "F16", { "sketchPlane" : qUnion([Q0])});
            skCircle(sketch, "E79", {"center": v(0, 120) * mm, "radius": 6 * mm});
            skLineSegment(sketch, "E80.0", {"start": v(-70, 90) * mm, "end": v(70, 90) * mm});
            skCircle(sketch, "E80.1", {"center": v(-60, 67.5) * mm, "radius": 4 * mm});
            skArc(sketch, "E80.2", {"start": v(80, 80) * mm, "mid": v(77.07, 87.07) * mm, "end": v(70, 90) * mm});
            skArc(sketch, "E80.3", {"start": v(-70, 90) * mm, "mid": v(-77.07, 87.07) * mm, "end": v(-80, 80) * mm});
            skCircle(sketch, "E80.4", {"center": v(60, 67.5) * mm, "radius": 4 * mm});
            skLineSegment(sketch, "E81", {"start": v(0, 90) * mm, "end": v(0, 120) * mm, "construction": true});
            skLineSegment(sketch, "E82", {"start": v(-33, 90) * mm, "end": v(-15, 108) * mm});
            skLineSegment(sketch, "E83", {"start": v(-15, 108) * mm, "end": v(-15, 120) * mm});
            skLineSegment(sketch, "E84", {"start": v(15, 120) * mm, "end": v(15, 108) * mm});
            skLineSegment(sketch, "E85", {"start": v(15, 108) * mm, "end": v(33, 90) * mm});
            skArc(sketch, "E86", {"start": v(15, 120) * mm, "mid": v(0, 135) * mm, "end": v(-15, 120) * mm});
            skLineSegment(sketch, "E87.0", {"start": v(-80, -80) * mm, "end": v(-80, 80) * mm});
            skLineSegment(sketch, "E88.0", {"start": v(-70, -90) * mm, "end": v(70, -90) * mm});
            skArc(sketch, "E88.1", {"start": v(-80, -80) * mm, "mid": v(-77.07, -87.07) * mm, "end": v(-70, -90) * mm});
            skArc(sketch, "E88.2", {"start": v(70, -90) * mm, "mid": v(77.07, -87.07) * mm, "end": v(80, -80) * mm});
            skLineSegment(sketch, "E88.3", {"start": v(80, -80) * mm, "end": v(80, 80) * mm});
            skLineSegment(sketch, "E89", {"start": v(-80, 0) * mm, "end": v(80, 0) * mm, "construction": true});
            skCircle(sketch, "E90.MirrorC", {"center": v(60, -67.5) * mm, "radius": 4 * mm});
            skLineSegment(sketch, "E91.MirrorCS", {"start": v(80, 80) * mm, "end": v(80, -80) * mm});
            skLineSegment(sketch, "E92.MirrorCS", {"start": v(-80, 80) * mm, "end": v(-80, -80) * mm});
            skLineSegment(sketch, "E93.MirrorCS", {"start": v(15, -120) * mm, "end": v(15, -108) * mm});
            skLineSegment(sketch, "E94.MirrorCS", {"start": v(-15, -108) * mm, "end": v(-15, -120) * mm});
            skArc(sketch, "E95.MirrorCS", {"start": v(15, -120) * mm, "mid": v(0, -135) * mm, "end": v(-15, -120) * mm});
            skLineSegment(sketch, "E96.MirrorCS", {"start": v(-33, -90) * mm, "end": v(-15, -108) * mm});
            skLineSegment(sketch, "E97.MirrorCS", {"start": v(0, -90) * mm, "end": v(0, -120) * mm, "construction": true});
            skArc(sketch, "E98.MirrorCS", {"start": v(-70, -90) * mm, "mid": v(-77.07, -87.07) * mm, "end": v(-80, -80) * mm});
            skLineSegment(sketch, "E99.MirrorCS", {"start": v(15, -108) * mm, "end": v(33, -90) * mm});
            skArc(sketch, "E100.MirrorCS", {"start": v(80, -80) * mm, "mid": v(77.07, -87.07) * mm, "end": v(70, -90) * mm});
            skCircle(sketch, "E101.MirrorC", {"center": v(-60, -67.5) * mm, "radius": 4 * mm});
            skCircle(sketch, "E102.MirrorC", {"center": v(0, -120) * mm, "radius": 6 * mm});
            skSolve(sketch);
        }
        {
            var Q0;
            Q0=makeQuery(id+"F16.imprint","IMPRINT",FACE,{"disambiguationData":[TD([[makeQuery(id+"F16.imprint","IMPRINT",EDGE,{"derivedFrom":sQuery(id+"F16.wireOp",EDGE,"E79")}),-1.0]])]});
            var Q1;
            Q1=makeQuery(id+"F16.imprint","IMPRINT",FACE,{"disambiguationData":[TD([[makeQuery(id+"F16.imprint","IMPRINT",EDGE,{"derivedFrom":sQuery(id+"F16.wireOp",EDGE,"E80.1")}),-1.0]])]});
            var Q2;
            Q2=makeQuery(id+"F16.imprint","IMPRINT",FACE,{"disambiguationData":[TD([[makeQuery(id+"F16.imprint","IMPRINT",EDGE,{"derivedFrom":sQuery(id+"F16.wireOp",EDGE,"E93.MirrorCS")}),1.0]])]});
            var Q3;
            Q3=makeQuery(id+"F2.opExtrude","CAP_FACE",FACE,{"disambiguationData":[OSD([sQuery(id+"F0.wireOp",EDGE,"E12"),sQuery(id+"F0.wireOp",EDGE,"E13"),sQuery(id+"F0.wireOp",EDGE,"E14"),sQuery(id+"F0.wireOp",EDGE,"E15"),sQuery(id+"F0.wireOp",EDGE,"E17.filletArc"),sQuery(id+"F0.wireOp",EDGE,"E18.filletArc"),sQuery(id+"F0.wireOp",EDGE,"E19.filletArc"),sQuery(id+"F0.wireOp",EDGE,"E20.filletArc"),sQuery(id+"F0.wireOp",EDGE,"E25.0"),sQuery(id+"F0.wireOp",EDGE,"E25.1"),sQuery(id+"F0.wireOp",EDGE,"E25.2"),sQuery(id+"F0.wireOp",EDGE,"E25.3"),sQuery(id+"F0.wireOp",EDGE,"E25.4"),sQuery(id+"F0.wireOp",EDGE,"E25.5"),sQuery(id+"F0.wireOp",EDGE,"E25.6"),sQuery(id+"F0.wireOp",EDGE,"E25.7")])],"isStart":false});
            extrude(context, id + "F17", {"entities" : qUnion([Q0, Q1, Q2]), "endBound" : BoundingType.UP_TO_SURFACE, "depth" : 25 * mm, "endBoundEntityFace" : qUnion([Q3]), "offsetDistance" : 25 * mm});
        }
    });
